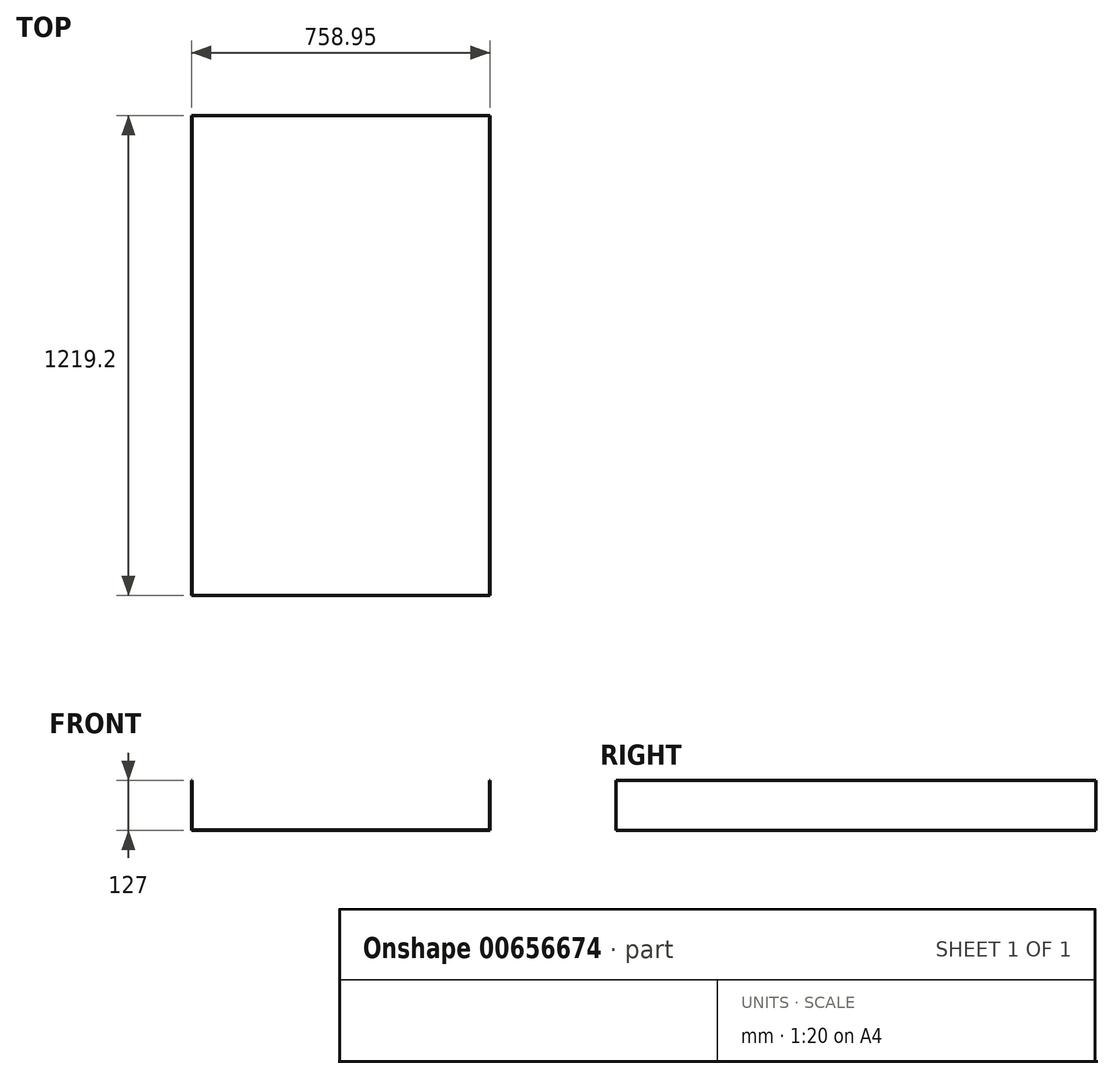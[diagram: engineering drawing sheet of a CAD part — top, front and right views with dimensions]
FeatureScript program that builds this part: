
annotation { "Feature Type Name" : "Feature", "Feature Type Description" : "" }
export const myFeature = defineFeature(function(context is Context, id is Id, definition is map)
    precondition{}
    {
        {
            var Q0;
            Q0=qCreatedBy(makeId("Front.planeOp"),FACE);
            var sketch = newSketch(context, id + "F0", { "sketchPlane" : qUnion([Q0])});
            skLineSegment(sketch, "E0", {"start": v(1.65, 127) * mm, "end": v(1.65, 1.65) * mm});
            skLineSegment(sketch, "E1", {"start": v(1.65, 1.65) * mm, "end": v(757.3, 1.65) * mm});
            skLineSegment(sketch, "E2", {"start": v(757.3, 1.65) * mm, "end": v(757.3, 127) * mm});
            skLineSegment(sketch, "E3.0", {"start": v(758.95, 0) * mm, "end": v(758.95, 127) * mm});
            skLineSegment(sketch, "E3.1", {"start": v(0, 0) * mm, "end": v(758.95, 0) * mm});
            skLineSegment(sketch, "E3.2", {"start": v(0, 127) * mm, "end": v(0, 0) * mm});
            skLineSegment(sketch, "E4", {"start": v(757.3, 127) * mm, "end": v(758.95, 127) * mm});
            skLineSegment(sketch, "E5", {"start": v(1.65, 127) * mm, "end": v(0, 127) * mm});
            skSolve(sketch);
        }
        {
            var Q0;
            Q0=makeQuery(id+"F0.imprint","IMPRINT",FACE,{"disambiguationData":[TD([[makeQuery(id+"F0.imprint","IMPRINT",EDGE,{"derivedFrom":sQuery(id+"F0.wireOp",EDGE,"E0")}),-1.0]])]});
            extrude(context, id + "F1", {"entities" : qUnion([Q0]), "depth" : 1219.2 * mm, "offsetDistance" : 25.4 * mm});
        }
    });
